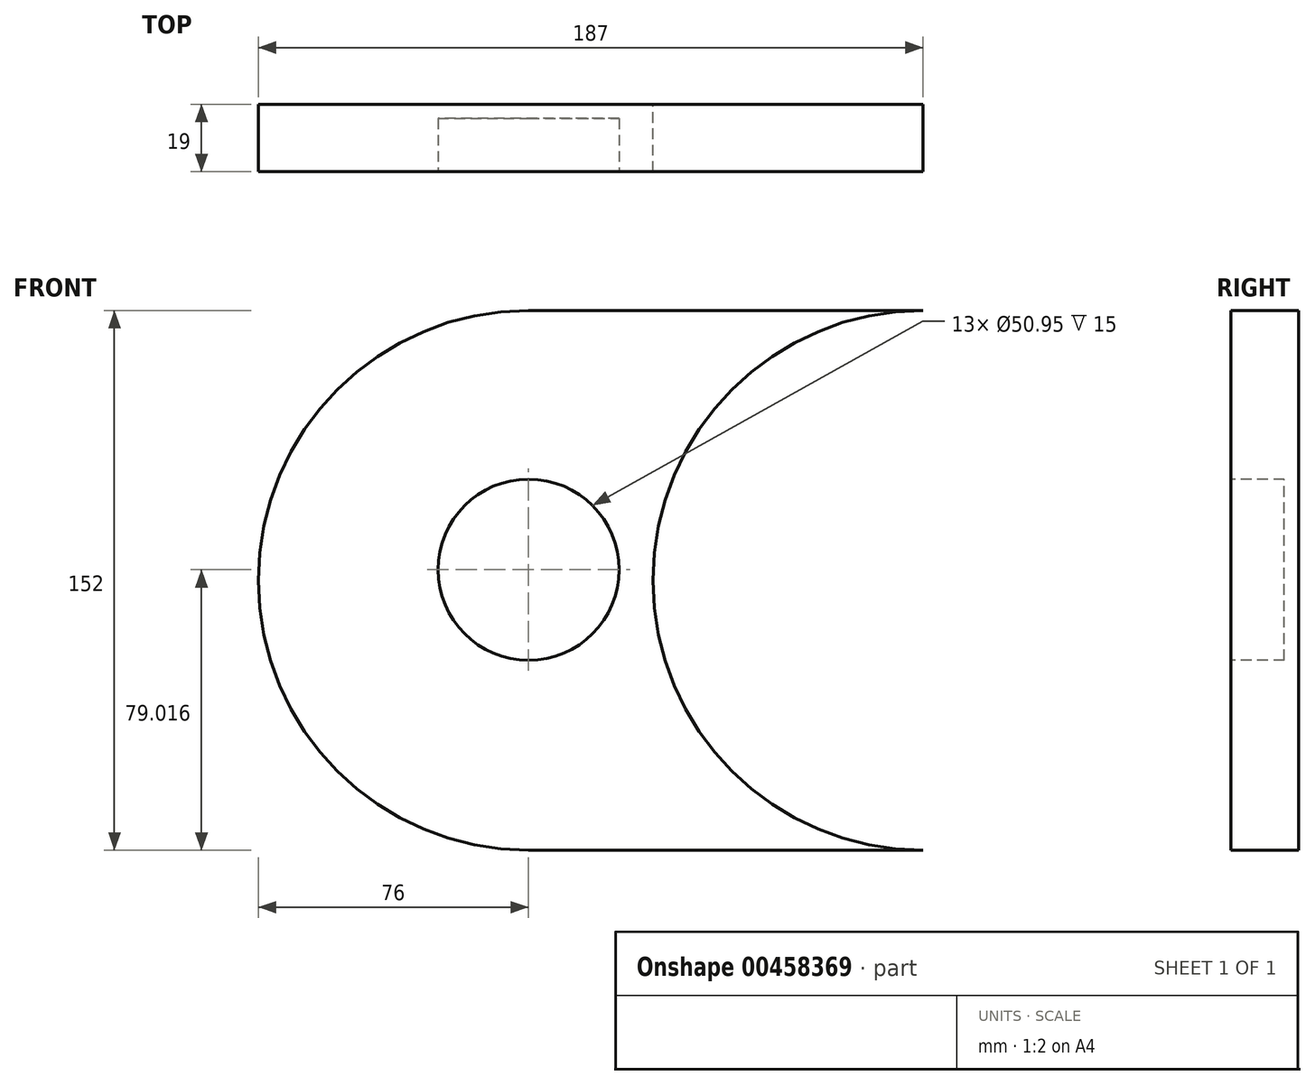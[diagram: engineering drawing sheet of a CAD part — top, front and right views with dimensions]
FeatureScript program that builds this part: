
annotation { "Feature Type Name" : "Feature", "Feature Type Description" : "" }
export const myFeature = defineFeature(function(context is Context, id is Id, definition is map)
    precondition{}
    {
        {
            var Q0;
            Q0=qCreatedBy(makeId("Front.planeOp"),FACE);
            var sketch = newSketch(context, id + "F0", { "sketchPlane" : qUnion([Q0])});
            skCircle(sketch, "E0", {"center": v(0, 0) * mm, "radius": 76 * mm});
            skCircle(sketch, "E1", {"center": v(111, 0) * mm, "radius": 76 * mm});
            skLineSegment(sketch, "E2", {"start": v(0, 76) * mm, "end": v(111, 76) * mm});
            skLineSegment(sketch, "E3", {"start": v(0, -76) * mm, "end": v(111, -76) * mm});
            skSolve(sketch);
        }
        {
            var Q0;
            {var subQ0=sQuery(id+"F0.wireOp",EDGE,"E2");Q0=makeQuery(id+"F0.imprint","IMPRINT",FACE,{"disambiguationData":[TD([[makeQuery(id+"F0.imprint","IMPRINT",EDGE,{"derivedFrom":subQ0}),-1.0]])]});}
            var Q1;
            {var subQ0=sQuery(id+"F0.wireOp",EDGE,"E0");var subQ1=makeQuery(id+"F0.imprint","INTERSECT",VERTEX,{"derivedFrom":[subQ0,sQuery(id+"F0.wireOp",EDGE,"E2")]});Q1=makeQuery(id+"F0.imprint","IMPRINT",FACE,{"disambiguationData":[TD([[makeQuery(id+"F0.imprint","IMPRINT",EDGE,{"disambiguationData":[TD([[subQ1,1.0]])],"derivedFrom":subQ0}),1.0]])]});}
            var Q2;
            {var subQ0=sQuery(id+"F0.wireOp",EDGE,"E1");var subQ1=sQuery(id+"F0.wireOp",EDGE,"E0");var subQ2=makeQuery(id+"F0.imprint","INTERSECT",VERTEX,{"disambiguationData":[OD(0.0)],"derivedFrom":[subQ1,subQ0]});Q2=makeQuery(id+"F0.imprint","IMPRINT",FACE,{"disambiguationData":[TD([[makeQuery(id+"F0.imprint","IMPRINT",EDGE,{"disambiguationData":[TD([[subQ2,1.0]])],"derivedFrom":subQ1}),1.0]])]});}
            var Q3;
            {var subQ0=sQuery(id+"F0.wireOp",EDGE,"E1");var subQ1=sQuery(id+"F0.wireOp",EDGE,"E0");var subQ2=makeQuery(id+"F0.imprint","INTERSECT",VERTEX,{"disambiguationData":[OD(0.0)],"derivedFrom":[subQ1,subQ0]});Q3=makeQuery(id+"F0.imprint","IMPRINT",FACE,{"disambiguationData":[TD([[makeQuery(id+"F0.imprint","IMPRINT",EDGE,{"disambiguationData":[TD([[subQ2,1.0]])],"derivedFrom":subQ1}),-1.0]])]});}
            var Q4;
            {var subQ0=sQuery(id+"F0.wireOp",EDGE,"E3");Q4=makeQuery(id+"F0.imprint","IMPRINT",FACE,{"disambiguationData":[TD([[makeQuery(id+"F0.imprint","IMPRINT",EDGE,{"derivedFrom":subQ0}),1.0]])]});}
            extrude(context, id + "F1", {"entities" : qUnion([Q0, Q1, Q2, Q3, Q4]), "depth" : 50 * mm, "offsetDistance" : 25 * mm});
        }
        {
            var Q0;
            Q0=qCreatedBy(makeId("Front.planeOp"),FACE);
            cPlane(context, id + "F2", {"entities" : qUnion([Q0]), "cplaneType" : CPlaneType.OFFSET, "offset" : 19 * mm, "width" : 150 * mm, "height" : 150 * mm});
        }
        {
            var Q0;
            Q0=qCreatedBy(id+"F2.planeOp",FACE);
            var sketch = newSketch(context, id + "F3", { "sketchPlane" : qUnion([Q0])});
            skCircle(sketch, "E4", {"center": v(0, 0) * mm, "radius": 60 * mm});
            skCircle(sketch, "E5", {"center": v(111, 0) * mm, "radius": 60 * mm});
            skLineSegment(sketch, "E6", {"start": v(0, 60) * mm, "end": v(111, 60) * mm});
            skLineSegment(sketch, "E7", {"start": v(0, -60) * mm, "end": v(111, -60) * mm});
            skSolve(sketch);
        }
        {
            var Q0;
            Q0 = qSketchRegion(id + "F3", true);
            extrude(context, id + "F4", {"entities" : qUnion([Q0]), "operationType" : NewBodyOperationType.REMOVE, "depth" : 31 * mm, "offsetDistance" : 25 * mm});
        }
        {
            var Q0;
            {var subQ0=sQuery(id+"F3.wireOp",EDGE,"E5");var subQ1=sQuery(id+"F3.wireOp",EDGE,"E4");var subQ2=makeQuery(id+"F3.imprint","INTERSECT",VERTEX,{"disambiguationData":[OD(0.0)],"derivedFrom":[subQ1,subQ0]});Q0=makeQuery(id+"F4.boolean.opBoolean","SPLIT",FACE,{"disambiguationData":[TD([makeQuery(id+"F4.opExtrude","SWEPT_FACE",FACE,{"disambiguationData":[OSD([subQ1]),TDD([makeQuery(id+"F3.imprint","IMPRINT",EDGE,{"disambiguationData":[TD([[subQ2,1.0]])],"derivedFrom":subQ1})])]})])],"derivedFrom":makeQuery(id+"F1.opExtrude","CAP_FACE",FACE,{"disambiguationData":[OSD([sQuery(id+"F0.wireOp",EDGE,"E0"),sQuery(id+"F0.wireOp",EDGE,"E1"),sQuery(id+"F0.wireOp",EDGE,"E2"),sQuery(id+"F0.wireOp",EDGE,"E3")])],"isStart":false})});}
            extrude(context, id + "F5", {"entities" : qUnion([Q0]), "operationType" : NewBodyOperationType.REMOVE, "oppositeDirection" : true, "depth" : 31 * mm, "offsetDistance" : 25 * mm});
        }
        {
            var Q0;
            Q0=qCreatedBy(id+"F2.planeOp",FACE);
            var sketch = newSketch(context, id + "F6", { "sketchPlane" : qUnion([Q0])});
            skCircle(sketch, "E8", {"center": v(0, 3.02) * mm, "radius": 25.47 * mm});
            skSolve(sketch);
        }
        {
            var Q0;
            Q0 = qSketchRegion(id + "F6", true);
            extrude(context, id + "F7", {"entities" : qUnion([Q0]), "operationType" : NewBodyOperationType.REMOVE, "oppositeDirection" : true, "depth" : 15 * mm, "offsetDistance" : 25 * mm});
        }
        {
            var Q0;
            Q0=qCreatedBy(makeId("Right.planeOp"),FACE);
            cPlane(context, id + "F8", {"entities" : qUnion([Q0]), "cplaneType" : CPlaneType.OFFSET, "offset" : 111 * mm, "width" : 150 * mm, "height" : 150 * mm});
        }
        {
            var Q0;
            Q0=qCreatedBy(id+"F8.planeOp",FACE);
            var sketch = newSketch(context, id + "F9", { "sketchPlane" : qUnion([Q0])});
            skLineSegment(sketch, "E9", {"start": v(0, 0) * mm, "end": v(0, 11) * mm});
            skLineSegment(sketch, "E10", {"start": v(0, 0) * mm, "end": v(-19, 0) * mm});
            skLineSegment(sketch, "E11", {"start": v(-19, 0) * mm, "end": v(-19, 23.5) * mm});
            skLineSegment(sketch, "E12", {"start": v(-19, 23.5) * mm, "end": v(-7, 23.5) * mm});
            skLineSegment(sketch, "E13", {"start": v(-7, 23.5) * mm, "end": v(-7, 18.5) * mm});
            skLineSegment(sketch, "E14", {"start": v(-7, 18.5) * mm, "end": v(-2, 18.5) * mm});
            skLineSegment(sketch, "E15", {"start": v(-2, 18.5) * mm, "end": v(-2, 11) * mm});
            skLineSegment(sketch, "E16", {"start": v(-2, 11) * mm, "end": v(0, 11) * mm});
            skLineSegment(sketch, "E17", {"start": v(0, 0) * mm, "end": v(-25.36, 0) * mm, "construction": true});
            skSolve(sketch);
        }
        {
            var Q0;
            Q0 = qSketchRegion(id + "F9", true);
            var Q1;
            Q1=sQuery(id+"F9.wireOp",EDGE,"E17");
            revolve(context, id + "F10", {"operationType" : NewBodyOperationType.REMOVE, "entities" : qUnion([Q0]), "axis" : qUnion([Q1]), "revolveType" : RevolveType.FULL, "oppositeDirection" : true});
        }
    });
